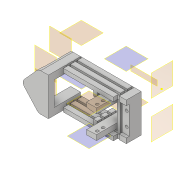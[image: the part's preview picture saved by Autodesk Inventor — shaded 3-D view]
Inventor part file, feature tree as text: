
AUTODESK INVENTOR PART (.ipt)
format: ipt  version: 2019.4 (Build 234330000, 330)  size: 519,168 bytes
history: native  units: mm
features: plane x15, sketch x14, extrude x13, projected_geometry x11, other x2, mirror x1, fillet x1
ambient origin geometry x8: Origin, YZ Plane, XZ Plane, XY Plane, X Axis, Y Axis, Z Axis, Center Point
bodies: Solid1 (feature_tree)
feature tree (57):
  plane  "Work Plane1"
  plane  "Work Plane2"
  plane  "Work Plane4"
  extrude  "Extrusion4"  Depth=4.0mm TaperAngle=0.0deg
  plane  "Work Plane5"
  extrude  "Extrusion5"  Depth=5.0mm TaperAngle=0.0deg
  plane  "Work Plane11"
  extrude  "Extrusion8"  Depth=5.0mm
  plane  "Work Plane7"
  extrude  "Extrusion9"  Depth=2.0mm
  plane  "Work Plane3"
  plane  "Work Plane13"
  extrude  "Extrusion10"  Depth=0.6mm
  plane  "Work Plane12"
  extrude  "Extrusion11"  Depth=4.0mm
  extrude  "Extrusion14"  Depth=1.0mm
  extrude  "Extrusion15"  Depth=2.9mm
  mirror  "Mirror2"
  extrude  "Extrusion17"  TaperAngle=0.0deg  [1 undecoded]
  extrude  "Extrusion18"  TaperAngle=0.0deg  [1 undecoded]
  sketch  "Sketch20"  dims[d101=7.0mm d102=0.0mm]
  extrude  "Extrusion19"  TaperAngle=0.0deg  [1 undecoded]
  extrude  "Extrusion20"  Depth=19.0mm
  fillet  "Fillet1"  Radius=22.0mm
  extrude  "Extrusion21"  Depth=4.0mm
  sketch  "Sketch5"  dims[d28=15.0mm d29=0.0mm d37=4.0mm d38=0.0mm]
  sketch  "Sketch6"  dims[d43=7.0mm d60=5.0mm d61=0.0mm]
  sketch  "Sketch9"  dims[d62=4.0mm d63=5.0mm]
  sketch  "Sketch10"  dims[d64=9.0mm d65=0.0mm d66=2.0mm]
  sketch  "Sketch11"  dims[d67=0.6mm d68=0.6mm]
  projected_geometry  "Projected Loop9"
  sketch  "Sketch12"  dims[d70=15.0mm d71=0.0mm d72=4.0mm]
  projected_geometry  "Projected Loop10"
  sketch  "Sketch15"  dims[d73=0.0mm d77=1.0mm]
  projected_geometry  "Projected Loop13"
  projected_geometry  "Projected Loop14"
  projected_geometry  "Projected Loop15"
  sketch  "Sketch16"  dims[d78=2.9mm d79=2.9mm]
  projected_geometry  "Projected Loop16"
  plane  "Work Plane14"
  plane  "Work Plane15"
  plane  "Work Plane16"
  plane  "Work Plane17"
  plane  "Work Plane18"
  plane  "Work Plane19"
  sketch  "Sketch18"  dims[d80=4.0mm d81=0.0mm d92=0.0mm]
  sketch  "Sketch19"  dims[d93=5.0mm d94=0.0mm]
  sketch  "Sketch21"  dims[d104=10.0mm d105=0.0mm d106=19.0mm d107=22.0mm]
  projected_geometry  "Projected Loop17"
  projected_geometry  "Projected Loop18"
  projected_geometry  "Projected Loop19"
  sketch  "Sketch22"  dims[d108=28.0mm d109=4.0mm]
  projected_geometry  "Projected Loop20"
  sketch  "Sketch23"  dims[d110=4.0mm d111=0.0mm d112=2.0mm d113=0.6mm d115=5.0mm d117=2.9mm d118=7.0mm d119=10.0mm d120=0.0mm d121=4.0mm d122=5.0mm d123=0.6mm d124=2.0mm d125=2.0mm d130=10.0mm d131=0.0mm d132=1.0mm d133=0.0mm d134=30.0mm d135=8.0mm d136=0.0mm d137=0.0mm d138=10.0mm d139=0.0mm d140=5.0mm d141=30.0mm d143=7.0mm d144=10.0mm d146=10.0mm d148=17.0mm d149=0.0mm d150=16.0mm d151=0.0mm d152=0.0mm d153=5.0mm d154=10.0mm d155=0.0mm]
  projected_geometry  "Projected Loop21"
  other  "Assembly_Opentrons_Autofocus_v2.iam"
  other  "00_MGN12C, LINEAR GUIDE BLOCK:1"
note: 3 required parameter values undecoded (feature->parameter linkage not recoverable at this tier; creation-order binding heuristic only, values carry confidence <= 0.55)
